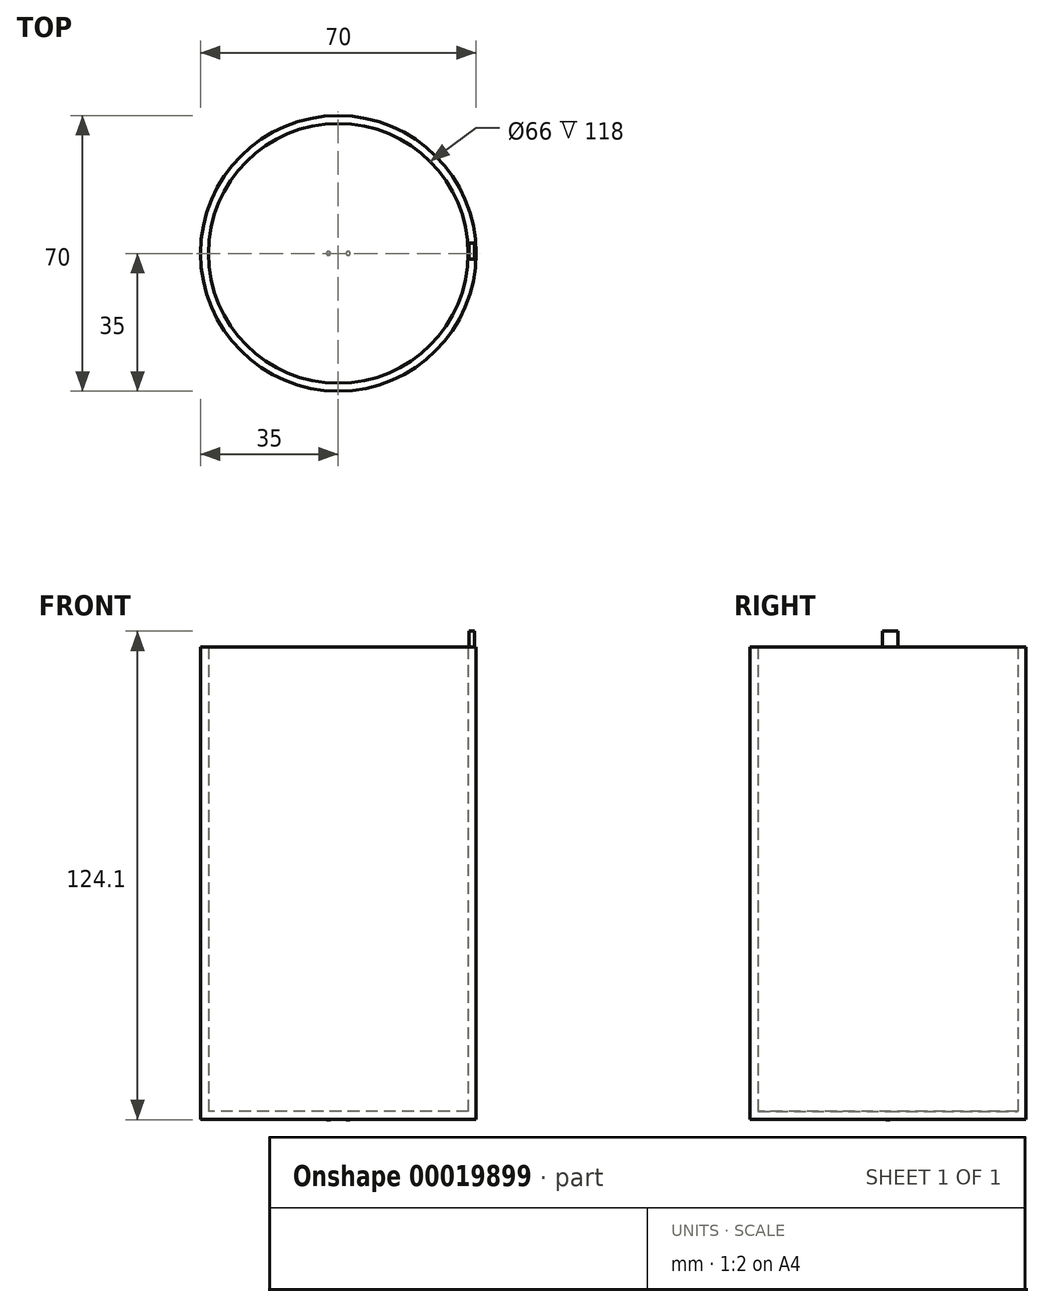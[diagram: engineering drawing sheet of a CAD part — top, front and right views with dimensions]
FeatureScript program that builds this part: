
annotation { "Feature Type Name" : "Feature", "Feature Type Description" : "" }
export const myFeature = defineFeature(function(context is Context, id is Id, definition is map)
    precondition{}
    {
        {
            var Q0;
            Q0=qCreatedBy(makeId("Top.planeOp"),FACE);
            var sketch = newSketch(context, id + "F0", { "sketchPlane" : qUnion([Q0])});
            skCircle(sketch, "E0", {"center": v(0, 0) * mm, "radius": 35 * mm});
            skSolve(sketch);
        }
        {
            var Q0;
            Q0 = qSketchRegion(id + "F0", true);
            extrude(context, id + "F1", {"entities" : qUnion([Q0]), "depth" : 120 * mm});
        }
        {
            var Q0;
            Q0=makeQuery(id+"F1.opExtrude","CAP_FACE",FACE,{"disambiguationData":[OSD([sQuery(id+"F0.wireOp",EDGE,"E0")])],"isStart":false});
            shell(context, id + "F2", {"entities" : qUnion([Q0]), "thickness" : 2 * mm});
        }
        {
            var Q0;
            Q0=makeQuery(id+"F1.opExtrude","CAP_FACE",FACE,{"disambiguationData":[OSD([sQuery(id+"F0.wireOp",EDGE,"E0")])],"isStart":true});
            var sketch = newSketch(context, id + "F3", { "sketchPlane" : qUnion([Q0])});
            skLineSegment(sketch, "E1", {"start": v(0, 0) * mm, "end": v(2.5, 0) * mm});
            skLineSegment(sketch, "E2", {"start": v(0, 0) * mm, "end": v(-2.5, 0) * mm});
            skCircle(sketch, "E3", {"center": v(-2.5, 0) * mm, "radius": 0.5 * mm});
            skCircle(sketch, "E4", {"center": v(2.5, 0) * mm, "radius": 0.5 * mm});
            skSolve(sketch);
        }
        {
            var Q0;
            Q0 = qSketchRegion(id + "F3", true);
            extrude(context, id + "F4", {"entities" : qUnion([Q0]), "operationType" : NewBodyOperationType.ADD, "depth" : 0.1 * mm});
        }
        {
            var Q0;
            Q0=makeQuery(id+"F1.opExtrude","CAP_FACE",FACE,{"disambiguationData":[OSD([sQuery(id+"F0.wireOp",EDGE,"E0")])],"isStart":false});
            var sketch = newSketch(context, id + "F5", { "sketchPlane" : qUnion([Q0])});
            skLineSegment(sketch, "E5.bottom", {"start": v(33.25, 2.57) * mm, "end": v(34.65, 2.57) * mm});
            skLineSegment(sketch, "E5.top", {"start": v(33.25, -1.43) * mm, "end": v(34.65, -1.43) * mm});
            skLineSegment(sketch, "E5.left", {"start": v(33.25, 2.57) * mm, "end": v(33.25, -1.43) * mm});
            skLineSegment(sketch, "E5.right", {"start": v(34.65, 2.57) * mm, "end": v(34.65, -1.43) * mm});
            skLineSegment(sketch, "E6", {"start": v(0, 0) * mm, "end": v(35.95, 0) * mm});
            skLineSegment(sketch, "E7", {"start": v(33.86, 0) * mm, "end": v(33.86, -1.43) * mm});
            skSolve(sketch);
        }
        {
            var Q0;
            Q0 = qSketchRegion(id + "F5", true);
            extrude(context, id + "F6", {"entities" : qUnion([Q0]), "operationType" : NewBodyOperationType.ADD, "depth" : 4 * mm});
        }
    });
